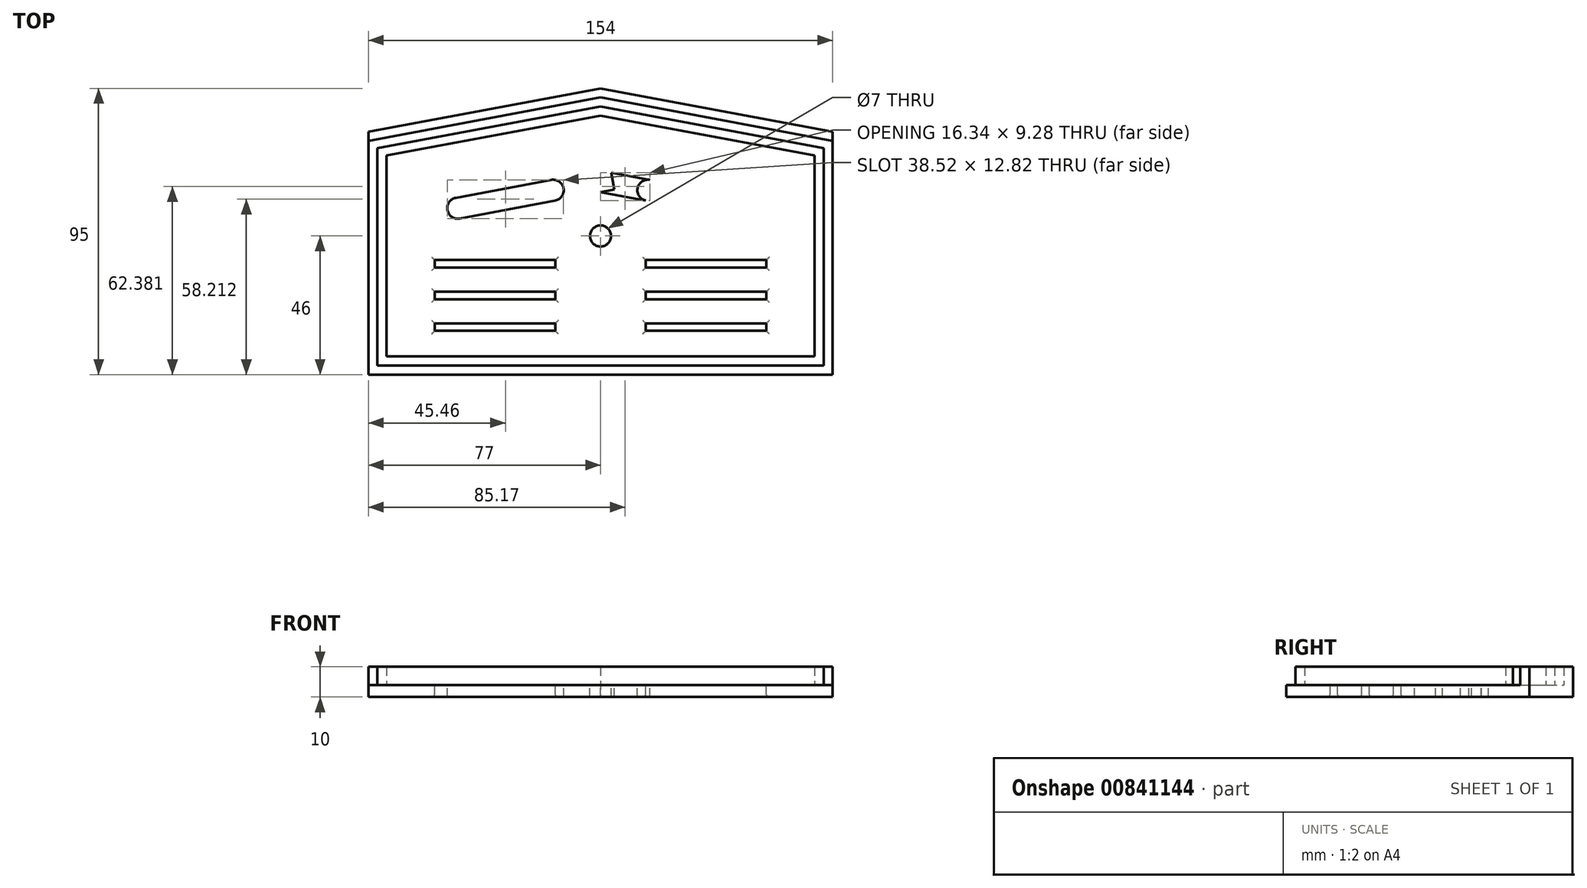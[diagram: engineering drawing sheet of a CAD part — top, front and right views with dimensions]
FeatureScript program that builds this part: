
annotation { "Feature Type Name" : "Feature", "Feature Type Description" : "" }
export const myFeature = defineFeature(function(context is Context, id is Id, definition is map)
    precondition{}
    {
        {
            var Q0;
            Q0=qCreatedBy(makeId("Top.planeOp"),FACE);
            var sketch = newSketch(context, id + "F0", { "sketchPlane" : qUnion([Q0])});
            skLineSegment(sketch, "E0.bottom", {"start": v(80, -49) * mm, "end": v(-80, -49) * mm});
            skLineSegment(sketch, "E0.top", {"start": v(80, 49) * mm, "end": v(-80, 49) * mm, "construction": true});
            skLineSegment(sketch, "E0.left", {"start": v(80, -49) * mm, "end": v(80, 49) * mm});
            skLineSegment(sketch, "E0.right", {"start": v(-80, -49) * mm, "end": v(-80, 49) * mm});
            skPoint(sketch, "E0.middle", {"position": v(0, 0) * mm});
            skLineSegment(sketch, "E1.bottom", {"start": v(-80, -49) * mm, "end": v(80, -49) * mm});
            skLineSegment(sketch, "E1.left", {"start": v(-80, -49) * mm, "end": v(-80, 85) * mm});
            skLineSegment(sketch, "E1.right", {"start": v(80, -49) * mm, "end": v(80, 43) * mm});
            skLineSegment(sketch, "E2.bottom", {"start": v(77, -46) * mm, "end": v(-77, -46) * mm});
            skLineSegment(sketch, "E2.top", {"start": v(77, 46) * mm, "end": v(-77, 46) * mm, "construction": true});
            skLineSegment(sketch, "E2.left", {"start": v(77, -46) * mm, "end": v(77, 46) * mm});
            skLineSegment(sketch, "E2.right", {"start": v(-77, -46) * mm, "end": v(-77, 46) * mm});
            skLineSegment(sketch, "E3.bottom", {"start": v(74, -43) * mm, "end": v(-74, -43) * mm});
            skLineSegment(sketch, "E3.top", {"start": v(74, 43) * mm, "end": v(-74, 43) * mm, "construction": true});
            skLineSegment(sketch, "E3.left", {"start": v(74, -43) * mm, "end": v(74, 43) * mm});
            skLineSegment(sketch, "E3.right", {"start": v(-74, -43) * mm, "end": v(-74, 43) * mm});
            skLineSegment(sketch, "E4.bottom", {"start": v(71, -40) * mm, "end": v(-71, -40) * mm});
            skLineSegment(sketch, "E4.top", {"start": v(71, 40) * mm, "end": v(-71, 40) * mm, "construction": true});
            skLineSegment(sketch, "E4.left", {"start": v(71, -40) * mm, "end": v(71, 40) * mm});
            skLineSegment(sketch, "E4.right", {"start": v(-71, -40) * mm, "end": v(-71, 40) * mm});
            skLineSegment(sketch, "E5.bottom", {"start": v(-80, 49) * mm, "end": v(80, 49) * mm, "construction": true});
            skLineSegment(sketch, "E5.top", {"start": v(-80, 34) * mm, "end": v(80, 34) * mm, "construction": true});
            skLineSegment(sketch, "E5.left", {"start": v(-80, 49) * mm, "end": v(-80, 34) * mm, "construction": true});
            skLineSegment(sketch, "E5.right", {"start": v(80, 49) * mm, "end": v(80, 34) * mm, "construction": true});
            skLineSegment(sketch, "E6", {"start": v(0, 49) * mm, "end": v(0, -49) * mm, "construction": true});
            skLineSegment(sketch, "E7", {"start": v(0, 49) * mm, "end": v(-80, 34) * mm});
            skLineSegment(sketch, "E8", {"start": v(0, 46) * mm, "end": v(-80, 31) * mm});
            skLineSegment(sketch, "E9", {"start": v(0, 43) * mm, "end": v(-80, 28) * mm});
            skLineSegment(sketch, "E10", {"start": v(0, 40) * mm, "end": v(-80, 25) * mm});
            skLineSegment(sketch, "E11", {"start": v(0, 49) * mm, "end": v(80, 34) * mm});
            skLineSegment(sketch, "E12", {"start": v(0, 46) * mm, "end": v(80, 31) * mm});
            skLineSegment(sketch, "E13", {"start": v(0, 43) * mm, "end": v(80, 28) * mm});
            skLineSegment(sketch, "E14", {"start": v(0, 40) * mm, "end": v(80, 25) * mm});
            skSolve(sketch);
        }
        {
            var Q0;
            {var subQ6=sQuery(id+"F0.wireOp",EDGE,"E4.bottom");Q0=makeQuery(id+"F0.imprint","IMPRINT",FACE,{"disambiguationData":[TD([[makeQuery(id+"F0.imprint","IMPRINT",EDGE,{"derivedFrom":subQ6}),-1.0]])]});}
            var Q1;
            {var subQ2=sQuery(id+"F0.wireOp",EDGE,"E2.bottom");Q1=makeQuery(id+"F0.imprint","IMPRINT",FACE,{"disambiguationData":[TD([[makeQuery(id+"F0.imprint","IMPRINT",EDGE,{"derivedFrom":subQ2}),-1.0]])]});}
            var Q2;
            {var subQ0=sQuery(id+"F0.wireOp",EDGE,"E13");var subQ9=sQuery(id+"F0.wireOp",EDGE,"E4.left");var subQ11=makeQuery(id+"F0.imprint","INTERSECT",VERTEX,{"derivedFrom":[subQ9,subQ0]});Q2=makeQuery(id+"F0.imprint","IMPRINT",FACE,{"disambiguationData":[TD([[makeQuery(id+"F0.imprint","IMPRINT",EDGE,{"disambiguationData":[TD([[subQ11,-1.0]])],"derivedFrom":subQ9}),1.0]])]});}
            var Q3;
            {var subQ2=sQuery(id+"F0.wireOp",EDGE,"E1.bottom");Q3=makeQuery(id+"F0.imprint","IMPRINT",FACE,{"disambiguationData":[TD([[makeQuery(id+"F0.imprint","IMPRINT",EDGE,{"derivedFrom":subQ2}),1.0]])]});}
            var Q4;
            {var subQ7=sQuery(id+"F0.wireOp",EDGE,"E3.bottom");Q4=makeQuery(id+"F0.imprint","IMPRINT",FACE,{"disambiguationData":[TD([[makeQuery(id+"F0.imprint","IMPRINT",EDGE,{"derivedFrom":subQ7}),-1.0]])]});}
            var Q5;
            {var subQ0=sQuery(id+"F0.wireOp",EDGE,"E8");var subQ1=sQuery(id+"F0.wireOp",EDGE,"E1.left");var subQ2=makeQuery(id+"F0.imprint","INTERSECT",VERTEX,{"derivedFrom":[subQ1,subQ0]});Q5=makeQuery(id+"F0.imprint","IMPRINT",FACE,{"disambiguationData":[TD([[makeQuery(id+"F0.imprint","IMPRINT",EDGE,{"disambiguationData":[TD([[subQ2,1.0]])],"derivedFrom":subQ1}),-1.0]])]});}
            var Q6;
            {var subQ0=sQuery(id+"F0.wireOp",EDGE,"E7");var subQ1=sQuery(id+"F0.wireOp",EDGE,"E1.left");var subQ2=makeQuery(id+"F0.imprint","INTERSECT",VERTEX,{"derivedFrom":[subQ1,subQ0]});Q6=makeQuery(id+"F0.imprint","IMPRINT",FACE,{"disambiguationData":[TD([[makeQuery(id+"F0.imprint","IMPRINT",EDGE,{"disambiguationData":[TD([[subQ2,1.0]])],"derivedFrom":subQ1}),-1.0]])]});}
            var Q7;
            {var subQ0=sQuery(id+"F0.wireOp",EDGE,"E9");var subQ1=sQuery(id+"F0.wireOp",EDGE,"E1.left");var subQ2=makeQuery(id+"F0.imprint","INTERSECT",VERTEX,{"derivedFrom":[subQ1,subQ0]});Q7=makeQuery(id+"F0.imprint","IMPRINT",FACE,{"disambiguationData":[TD([[makeQuery(id+"F0.imprint","IMPRINT",EDGE,{"disambiguationData":[TD([[subQ2,1.0]])],"derivedFrom":subQ1}),-1.0]])]});}
            var Q8;
            {var subQ0=sQuery(id+"F0.wireOp",EDGE,"E7");var subQ1=sQuery(id+"F0.wireOp",EDGE,"E2.right");var subQ2=makeQuery(id+"F0.imprint","INTERSECT",VERTEX,{"derivedFrom":[subQ1,subQ0]});Q8=makeQuery(id+"F0.imprint","IMPRINT",FACE,{"disambiguationData":[TD([[makeQuery(id+"F0.imprint","IMPRINT",EDGE,{"disambiguationData":[TD([[subQ2,1.0]])],"derivedFrom":subQ1}),-1.0]])]});}
            var Q9;
            {var subQ0=sQuery(id+"F0.wireOp",EDGE,"E9");var subQ1=sQuery(id+"F0.wireOp",EDGE,"E2.right");var subQ2=makeQuery(id+"F0.imprint","INTERSECT",VERTEX,{"derivedFrom":[subQ1,subQ0]});Q9=makeQuery(id+"F0.imprint","IMPRINT",FACE,{"disambiguationData":[TD([[makeQuery(id+"F0.imprint","IMPRINT",EDGE,{"disambiguationData":[TD([[subQ2,-1.0]])],"derivedFrom":subQ1}),-1.0]])]});}
            var Q10;
            {var subQ0=sQuery(id+"F0.wireOp",EDGE,"E10");var subQ1=sQuery(id+"F0.wireOp",EDGE,"E2.right");var subQ2=makeQuery(id+"F0.imprint","INTERSECT",VERTEX,{"derivedFrom":[subQ1,subQ0]});Q10=makeQuery(id+"F0.imprint","IMPRINT",FACE,{"disambiguationData":[TD([[makeQuery(id+"F0.imprint","IMPRINT",EDGE,{"disambiguationData":[TD([[subQ2,-1.0]])],"derivedFrom":subQ1}),-1.0]])]});}
            var Q11;
            {var subQ0=sQuery(id+"F0.wireOp",EDGE,"E9");var subQ1=sQuery(id+"F0.wireOp",EDGE,"E3.right");var subQ2=makeQuery(id+"F0.imprint","INTERSECT",VERTEX,{"derivedFrom":[subQ1,subQ0]});Q11=makeQuery(id+"F0.imprint","IMPRINT",FACE,{"disambiguationData":[TD([[makeQuery(id+"F0.imprint","IMPRINT",EDGE,{"disambiguationData":[TD([[subQ2,-1.0]])],"derivedFrom":subQ1}),-1.0]])]});}
            var Q12;
            {var subQ0=sQuery(id+"F0.wireOp",EDGE,"E10");var subQ1=sQuery(id+"F0.wireOp",EDGE,"E3.right");var subQ2=makeQuery(id+"F0.imprint","INTERSECT",VERTEX,{"derivedFrom":[subQ1,subQ0]});Q12=makeQuery(id+"F0.imprint","IMPRINT",FACE,{"disambiguationData":[TD([[makeQuery(id+"F0.imprint","IMPRINT",EDGE,{"disambiguationData":[TD([[subQ2,-1.0]])],"derivedFrom":subQ1}),-1.0]])]});}
            var Q13;
            {var subQ0=sQuery(id+"F0.wireOp",EDGE,"E7");var subQ1=sQuery(id+"F0.wireOp",EDGE,"E3.right");var subQ2=makeQuery(id+"F0.imprint","INTERSECT",VERTEX,{"derivedFrom":[subQ1,subQ0]});Q13=makeQuery(id+"F0.imprint","IMPRINT",FACE,{"disambiguationData":[TD([[makeQuery(id+"F0.imprint","IMPRINT",EDGE,{"disambiguationData":[TD([[subQ2,1.0]])],"derivedFrom":subQ1}),-1.0]])]});}
            var Q14;
            {var subQ7=sQuery(id+"F0.wireOp",EDGE,"E11");var subQ9=sQuery(id+"F0.wireOp",EDGE,"E4.left");var subQ10=makeQuery(id+"F0.imprint","INTERSECT",VERTEX,{"derivedFrom":[subQ9,subQ7]});Q14=makeQuery(id+"F0.imprint","IMPRINT",FACE,{"disambiguationData":[TD([[makeQuery(id+"F0.imprint","IMPRINT",EDGE,{"disambiguationData":[TD([[subQ10,1.0]])],"derivedFrom":subQ9}),1.0]])]});}
            var Q15;
            {var subQ0=sQuery(id+"F0.wireOp",EDGE,"E14");var subQ9=sQuery(id+"F0.wireOp",EDGE,"E4.left");var subQ10=makeQuery(id+"F0.imprint","INTERSECT",VERTEX,{"derivedFrom":[subQ9,subQ0]});Q15=makeQuery(id+"F0.imprint","IMPRINT",FACE,{"disambiguationData":[TD([[makeQuery(id+"F0.imprint","IMPRINT",EDGE,{"disambiguationData":[TD([[subQ10,-1.0]])],"derivedFrom":subQ9}),1.0]])]});}
            var Q16;
            {var subQ0=sQuery(id+"F0.wireOp",EDGE,"E11");var subQ1=sQuery(id+"F0.wireOp",EDGE,"E3.left");var subQ2=makeQuery(id+"F0.imprint","INTERSECT",VERTEX,{"derivedFrom":[subQ1,subQ0]});Q16=makeQuery(id+"F0.imprint","IMPRINT",FACE,{"disambiguationData":[TD([[makeQuery(id+"F0.imprint","IMPRINT",EDGE,{"disambiguationData":[TD([[subQ2,1.0]])],"derivedFrom":subQ1}),1.0]])]});}
            var Q17;
            {var subQ0=sQuery(id+"F0.wireOp",EDGE,"E11");var subQ1=sQuery(id+"F0.wireOp",EDGE,"E2.left");var subQ2=makeQuery(id+"F0.imprint","INTERSECT",VERTEX,{"derivedFrom":[subQ1,subQ0]});Q17=makeQuery(id+"F0.imprint","IMPRINT",FACE,{"disambiguationData":[TD([[makeQuery(id+"F0.imprint","IMPRINT",EDGE,{"disambiguationData":[TD([[subQ2,1.0]])],"derivedFrom":subQ1}),1.0]])]});}
            var Q18;
            {var subQ0=sQuery(id+"F0.wireOp",EDGE,"E11");var subQ1=sQuery(id+"F0.wireOp",EDGE,"E1.right");var subQ2=makeQuery(id+"F0.imprint","INTERSECT",VERTEX,{"derivedFrom":[subQ1,subQ0]});Q18=makeQuery(id+"F0.imprint","IMPRINT",FACE,{"disambiguationData":[TD([[makeQuery(id+"F0.imprint","IMPRINT",EDGE,{"disambiguationData":[TD([[subQ2,1.0]])],"derivedFrom":subQ1}),1.0]])]});}
            var Q19;
            {var subQ0=sQuery(id+"F0.wireOp",EDGE,"E12");var subQ1=sQuery(id+"F0.wireOp",EDGE,"E1.right");var subQ2=makeQuery(id+"F0.imprint","INTERSECT",VERTEX,{"derivedFrom":[subQ1,subQ0]});Q19=makeQuery(id+"F0.imprint","IMPRINT",FACE,{"disambiguationData":[TD([[makeQuery(id+"F0.imprint","IMPRINT",EDGE,{"disambiguationData":[TD([[subQ2,1.0]])],"derivedFrom":subQ1}),1.0]])]});}
            var Q20;
            {var subQ0=sQuery(id+"F0.wireOp",EDGE,"E13");var subQ1=sQuery(id+"F0.wireOp",EDGE,"E1.right");var subQ2=makeQuery(id+"F0.imprint","INTERSECT",VERTEX,{"derivedFrom":[subQ1,subQ0]});Q20=makeQuery(id+"F0.imprint","IMPRINT",FACE,{"disambiguationData":[TD([[makeQuery(id+"F0.imprint","IMPRINT",EDGE,{"disambiguationData":[TD([[subQ2,1.0]])],"derivedFrom":subQ1}),1.0]])]});}
            var Q21;
            {var subQ0=sQuery(id+"F0.wireOp",EDGE,"E14");var subQ1=sQuery(id+"F0.wireOp",EDGE,"E2.left");var subQ2=makeQuery(id+"F0.imprint","INTERSECT",VERTEX,{"derivedFrom":[subQ1,subQ0]});Q21=makeQuery(id+"F0.imprint","IMPRINT",FACE,{"disambiguationData":[TD([[makeQuery(id+"F0.imprint","IMPRINT",EDGE,{"disambiguationData":[TD([[subQ2,-1.0]])],"derivedFrom":subQ1}),1.0]])]});}
            var Q22;
            {var subQ0=sQuery(id+"F0.wireOp",EDGE,"E14");var subQ1=sQuery(id+"F0.wireOp",EDGE,"E3.left");var subQ2=makeQuery(id+"F0.imprint","INTERSECT",VERTEX,{"derivedFrom":[subQ1,subQ0]});Q22=makeQuery(id+"F0.imprint","IMPRINT",FACE,{"disambiguationData":[TD([[makeQuery(id+"F0.imprint","IMPRINT",EDGE,{"disambiguationData":[TD([[subQ2,-1.0]])],"derivedFrom":subQ1}),1.0]])]});}
            var Q23;
            {var subQ0=sQuery(id+"F0.wireOp",EDGE,"E13");var subQ1=sQuery(id+"F0.wireOp",EDGE,"E3.left");var subQ2=makeQuery(id+"F0.imprint","INTERSECT",VERTEX,{"derivedFrom":[subQ1,subQ0]});Q23=makeQuery(id+"F0.imprint","IMPRINT",FACE,{"disambiguationData":[TD([[makeQuery(id+"F0.imprint","IMPRINT",EDGE,{"disambiguationData":[TD([[subQ2,-1.0]])],"derivedFrom":subQ1}),1.0]])]});}
            var Q24;
            {var subQ0=sQuery(id+"F0.wireOp",EDGE,"E13");var subQ1=sQuery(id+"F0.wireOp",EDGE,"E2.left");var subQ2=makeQuery(id+"F0.imprint","INTERSECT",VERTEX,{"derivedFrom":[subQ1,subQ0]});Q24=makeQuery(id+"F0.imprint","IMPRINT",FACE,{"disambiguationData":[TD([[makeQuery(id+"F0.imprint","IMPRINT",EDGE,{"disambiguationData":[TD([[subQ2,-1.0]])],"derivedFrom":subQ1}),1.0]])]});}
            extrude(context, id + "F1", {"entities" : qUnion([Q0, Q1, Q2, Q3, Q4, Q5, Q6, Q7, Q8, Q9, Q10, Q11, Q12, Q13, Q14, Q15, Q16, Q17, Q18, Q19, Q20, Q21, Q22, Q23, Q24]), "depth" : 4 * mm, "offsetDistance" : 25 * mm});
        }
        {
            var Q0;
            {var subQ0=sQuery(id+"F0.wireOp",EDGE,"E11");var subQ1=sQuery(id+"F0.wireOp",EDGE,"E1.right");var subQ2=makeQuery(id+"F0.imprint","INTERSECT",VERTEX,{"derivedFrom":[subQ1,subQ0]});Q0=makeQuery(id+"F0.imprint","IMPRINT",FACE,{"disambiguationData":[TD([[makeQuery(id+"F0.imprint","IMPRINT",EDGE,{"disambiguationData":[TD([[subQ2,1.0]])],"derivedFrom":subQ1}),1.0]])]});}
            var Q1;
            {var subQ0=sQuery(id+"F0.wireOp",EDGE,"E11");var subQ1=sQuery(id+"F0.wireOp",EDGE,"E2.left");var subQ2=makeQuery(id+"F0.imprint","INTERSECT",VERTEX,{"derivedFrom":[subQ1,subQ0]});Q1=makeQuery(id+"F0.imprint","IMPRINT",FACE,{"disambiguationData":[TD([[makeQuery(id+"F0.imprint","IMPRINT",EDGE,{"disambiguationData":[TD([[subQ2,1.0]])],"derivedFrom":subQ1}),1.0]])]});}
            var Q2;
            {var subQ0=sQuery(id+"F0.wireOp",EDGE,"E11");var subQ1=sQuery(id+"F0.wireOp",EDGE,"E3.left");var subQ2=makeQuery(id+"F0.imprint","INTERSECT",VERTEX,{"derivedFrom":[subQ1,subQ0]});Q2=makeQuery(id+"F0.imprint","IMPRINT",FACE,{"disambiguationData":[TD([[makeQuery(id+"F0.imprint","IMPRINT",EDGE,{"disambiguationData":[TD([[subQ2,1.0]])],"derivedFrom":subQ1}),1.0]])]});}
            var Q3;
            {var subQ7=sQuery(id+"F0.wireOp",EDGE,"E11");var subQ9=sQuery(id+"F0.wireOp",EDGE,"E4.left");var subQ10=makeQuery(id+"F0.imprint","INTERSECT",VERTEX,{"derivedFrom":[subQ9,subQ7]});Q3=makeQuery(id+"F0.imprint","IMPRINT",FACE,{"disambiguationData":[TD([[makeQuery(id+"F0.imprint","IMPRINT",EDGE,{"disambiguationData":[TD([[subQ10,1.0]])],"derivedFrom":subQ9}),1.0]])]});}
            var Q4;
            {var subQ0=sQuery(id+"F0.wireOp",EDGE,"E7");var subQ1=sQuery(id+"F0.wireOp",EDGE,"E3.right");var subQ2=makeQuery(id+"F0.imprint","INTERSECT",VERTEX,{"derivedFrom":[subQ1,subQ0]});Q4=makeQuery(id+"F0.imprint","IMPRINT",FACE,{"disambiguationData":[TD([[makeQuery(id+"F0.imprint","IMPRINT",EDGE,{"disambiguationData":[TD([[subQ2,1.0]])],"derivedFrom":subQ1}),-1.0]])]});}
            var Q5;
            {var subQ0=sQuery(id+"F0.wireOp",EDGE,"E7");var subQ1=sQuery(id+"F0.wireOp",EDGE,"E2.right");var subQ2=makeQuery(id+"F0.imprint","INTERSECT",VERTEX,{"derivedFrom":[subQ1,subQ0]});Q5=makeQuery(id+"F0.imprint","IMPRINT",FACE,{"disambiguationData":[TD([[makeQuery(id+"F0.imprint","IMPRINT",EDGE,{"disambiguationData":[TD([[subQ2,1.0]])],"derivedFrom":subQ1}),-1.0]])]});}
            var Q6;
            {var subQ0=sQuery(id+"F0.wireOp",EDGE,"E7");var subQ1=sQuery(id+"F0.wireOp",EDGE,"E1.left");var subQ2=makeQuery(id+"F0.imprint","INTERSECT",VERTEX,{"derivedFrom":[subQ1,subQ0]});Q6=makeQuery(id+"F0.imprint","IMPRINT",FACE,{"disambiguationData":[TD([[makeQuery(id+"F0.imprint","IMPRINT",EDGE,{"disambiguationData":[TD([[subQ2,1.0]])],"derivedFrom":subQ1}),-1.0]])]});}
            var Q7;
            {var subQ0=sQuery(id+"F0.wireOp",EDGE,"E9");var subQ1=sQuery(id+"F0.wireOp",EDGE,"E1.left");var subQ2=makeQuery(id+"F0.imprint","INTERSECT",VERTEX,{"derivedFrom":[subQ1,subQ0]});Q7=makeQuery(id+"F0.imprint","IMPRINT",FACE,{"disambiguationData":[TD([[makeQuery(id+"F0.imprint","IMPRINT",EDGE,{"disambiguationData":[TD([[subQ2,1.0]])],"derivedFrom":subQ1}),-1.0]])]});}
            var Q8;
            {var subQ0=sQuery(id+"F0.wireOp",EDGE,"E10");var subQ1=sQuery(id+"F0.wireOp",EDGE,"E3.right");var subQ2=makeQuery(id+"F0.imprint","INTERSECT",VERTEX,{"derivedFrom":[subQ1,subQ0]});Q8=makeQuery(id+"F0.imprint","IMPRINT",FACE,{"disambiguationData":[TD([[makeQuery(id+"F0.imprint","IMPRINT",EDGE,{"disambiguationData":[TD([[subQ2,-1.0]])],"derivedFrom":subQ1}),-1.0]])]});}
            var Q9;
            {var subQ0=sQuery(id+"F0.wireOp",EDGE,"E14");var subQ9=sQuery(id+"F0.wireOp",EDGE,"E4.left");var subQ10=makeQuery(id+"F0.imprint","INTERSECT",VERTEX,{"derivedFrom":[subQ9,subQ0]});Q9=makeQuery(id+"F0.imprint","IMPRINT",FACE,{"disambiguationData":[TD([[makeQuery(id+"F0.imprint","IMPRINT",EDGE,{"disambiguationData":[TD([[subQ10,-1.0]])],"derivedFrom":subQ9}),1.0]])]});}
            var Q10;
            {var subQ0=sQuery(id+"F0.wireOp",EDGE,"E13");var subQ1=sQuery(id+"F0.wireOp",EDGE,"E1.right");var subQ2=makeQuery(id+"F0.imprint","INTERSECT",VERTEX,{"derivedFrom":[subQ1,subQ0]});Q10=makeQuery(id+"F0.imprint","IMPRINT",FACE,{"disambiguationData":[TD([[makeQuery(id+"F0.imprint","IMPRINT",EDGE,{"disambiguationData":[TD([[subQ2,1.0]])],"derivedFrom":subQ1}),1.0]])]});}
            var Q11;
            {var subQ0=sQuery(id+"F0.wireOp",EDGE,"E14");var subQ1=sQuery(id+"F0.wireOp",EDGE,"E3.left");var subQ2=makeQuery(id+"F0.imprint","INTERSECT",VERTEX,{"derivedFrom":[subQ1,subQ0]});Q11=makeQuery(id+"F0.imprint","IMPRINT",FACE,{"disambiguationData":[TD([[makeQuery(id+"F0.imprint","IMPRINT",EDGE,{"disambiguationData":[TD([[subQ2,-1.0]])],"derivedFrom":subQ1}),1.0]])]});}
            var Q12;
            {var subQ2=sQuery(id+"F0.wireOp",EDGE,"E1.bottom");Q12=makeQuery(id+"F0.imprint","IMPRINT",FACE,{"disambiguationData":[TD([[makeQuery(id+"F0.imprint","IMPRINT",EDGE,{"derivedFrom":subQ2}),1.0]])]});}
            var Q13;
            {var subQ7=sQuery(id+"F0.wireOp",EDGE,"E3.bottom");Q13=makeQuery(id+"F0.imprint","IMPRINT",FACE,{"disambiguationData":[TD([[makeQuery(id+"F0.imprint","IMPRINT",EDGE,{"derivedFrom":subQ7}),-1.0]])]});}
            var Q14;
            {var subQ0=sQuery(id+"F0.wireOp",EDGE,"E8");var subQ1=sQuery(id+"F0.wireOp",EDGE,"E1.left");var subQ2=makeQuery(id+"F0.imprint","INTERSECT",VERTEX,{"derivedFrom":[subQ1,subQ0]});Q14=makeQuery(id+"F0.imprint","IMPRINT",FACE,{"disambiguationData":[TD([[makeQuery(id+"F0.imprint","IMPRINT",EDGE,{"disambiguationData":[TD([[subQ2,1.0]])],"derivedFrom":subQ1}),-1.0]])]});}
            var Q15;
            {var subQ0=sQuery(id+"F0.wireOp",EDGE,"E12");var subQ1=sQuery(id+"F0.wireOp",EDGE,"E1.right");var subQ2=makeQuery(id+"F0.imprint","INTERSECT",VERTEX,{"derivedFrom":[subQ1,subQ0]});Q15=makeQuery(id+"F0.imprint","IMPRINT",FACE,{"disambiguationData":[TD([[makeQuery(id+"F0.imprint","IMPRINT",EDGE,{"disambiguationData":[TD([[subQ2,1.0]])],"derivedFrom":subQ1}),1.0]])]});}
            extrude(context, id + "F2", {"entities" : qUnion([Q0, Q1, Q2, Q3, Q4, Q5, Q6, Q7, Q8, Q9, Q10, Q11, Q12, Q13, Q14, Q15]), "operationType" : NewBodyOperationType.ADD, "depth" : 10 * mm, "offsetDistance" : 25 * mm});
        }
        {
            var Q0;
            Q0=makeQuery(id+"F2.boolean.opBoolean","SPLIT",FACE,{"disambiguationData":[TD([makeQuery(id+"F2.opExtrude","SWEPT_FACE",FACE,{"disambiguationData":[OSD([sQuery(id+"F0.wireOp",EDGE,"E4.bottom")])]})])],"derivedFrom":makeQuery(id+"F1.opExtrude","CAP_FACE",FACE,{"disambiguationData":[OSD([sQuery(id+"F0.wireOp",EDGE,"E1.bottom"),sQuery(id+"F0.wireOp",EDGE,"E1.left"),sQuery(id+"F0.wireOp",EDGE,"E1.right"),sQuery(id+"F0.wireOp",EDGE,"E7"),sQuery(id+"F0.wireOp",EDGE,"E11")])],"isStart":false})});
            var sketch = newSketch(context, id + "F3", { "sketchPlane" : qUnion([Q0])});
            skLineSegment(sketch, "E15", {"start": v(0, 0) * mm, "end": v(0, 40) * mm});
            skLineSegment(sketch, "E16", {"start": v(0, 40) * mm, "end": v(-71, 26.69) * mm});
            skLineSegment(sketch, "E17", {"start": v(-71, 26.69) * mm, "end": v(-71, 0) * mm});
            skLineSegment(sketch, "E18", {"start": v(-71, 0) * mm, "end": v(0, 0) * mm});
            skCircle(sketch, "E19", {"center": v(0, 0) * mm, "radius": 3.5 * mm});
            skLineSegment(sketch, "E20", {"start": v(-71, 26.69) * mm, "end": v(-67.68, 9) * mm});
            skLineSegment(sketch, "E21", {"start": v(0, 40) * mm, "end": v(3.32, 22.3) * mm});
            skLineSegment(sketch, "E22", {"start": v(3.32, 22.3) * mm, "end": v(-67.68, 9) * mm});
            skLineSegment(sketch, "E23", {"start": v(-67.68, 9) * mm, "end": v(-66.4, 2.12) * mm});
            skLineSegment(sketch, "E24", {"start": v(-66.4, 2.12) * mm, "end": v(4.6, 15.43) * mm});
            skLineSegment(sketch, "E25", {"start": v(4.6, 15.43) * mm, "end": v(3.32, 22.3) * mm});
            skLineSegment(sketch, "E26", {"start": v(-48.03, 12.68) * mm, "end": v(-46.74, 5.8) * mm});
            skLineSegment(sketch, "E27", {"start": v(-16.34, 18.62) * mm, "end": v(-15.05, 11.74) * mm});
            skArc(sketch, "E28", {"start": v(-48.03, 12.68) * mm, "mid": v(-50.8, 8.6) * mm, "end": v(-46.74, 5.8) * mm});
            skArc(sketch, "E29", {"start": v(-15.05, 11.74) * mm, "mid": v(-12.28, 15.82) * mm, "end": v(-16.34, 18.62) * mm});
            skArc(sketch, "E30.MirrorCS", {"start": v(15.05, 11.74) * mm, "mid": v(12.28, 15.82) * mm, "end": v(16.34, 18.62) * mm});
            skLineSegment(sketch, "E31.MirrorCS", {"start": v(-3.32, 22.3) * mm, "end": v(67.68, 9) * mm});
            skArc(sketch, "E32.MirrorCS", {"start": v(48.03, 12.68) * mm, "mid": v(50.8, 8.6) * mm, "end": v(46.74, 5.8) * mm});
            skLineSegment(sketch, "E33.MirrorCS", {"start": v(66.4, 2.12) * mm, "end": v(-4.6, 15.43) * mm});
            skSolve(sketch);
        }
        {
            var Q0;
            {var subQ0=sQuery(id+"F3.wireOp",EDGE,"E18");var subQ1=sQuery(id+"F3.wireOp",EDGE,"E15");var subQ2=makeQuery(id+"F3.imprint","INTERSECT",VERTEX,{"derivedFrom":[subQ1,subQ0]});Q0=makeQuery(id+"F3.imprint","IMPRINT",FACE,{"disambiguationData":[TD([[makeQuery(id+"F3.imprint","IMPRINT",EDGE,{"disambiguationData":[TD([[subQ2,-1.0]])],"derivedFrom":subQ1}),1.0]])]});}
            var Q1;
            {var subQ0=sQuery(id+"F3.wireOp",EDGE,"E18");var subQ1=sQuery(id+"F3.wireOp",EDGE,"E15");var subQ2=makeQuery(id+"F3.imprint","INTERSECT",VERTEX,{"derivedFrom":[subQ1,subQ0]});Q1=makeQuery(id+"F3.imprint","IMPRINT",FACE,{"disambiguationData":[TD([[makeQuery(id+"F3.imprint","IMPRINT",EDGE,{"disambiguationData":[TD([[subQ2,-1.0]])],"derivedFrom":subQ1}),-1.0]])]});}
            extrude(context, id + "F4", {"entities" : qUnion([Q0, Q1]), "operationType" : NewBodyOperationType.REMOVE, "oppositeDirection" : true, "depth" : 25 * mm, "offsetDistance" : 25 * mm});
        }
        {
            var Q0;
            Q0=makeQuery(id+"F3.imprint","IMPRINT",FACE,{"disambiguationData":[TD([[makeQuery(id+"F3.imprint","IMPRINT",EDGE,{"derivedFrom":sQuery(id+"F3.wireOp",EDGE,"E26")}),-1.0]])]});
            var Q1;
            {var subQ1=sQuery(id+"F3.wireOp",EDGE,"E26");Q1=makeQuery(id+"F3.imprint","IMPRINT",FACE,{"disambiguationData":[TD([[makeQuery(id+"F3.imprint","IMPRINT",EDGE,{"derivedFrom":subQ1}),1.0]])]});}
            var Q2;
            Q2=makeQuery(id+"F3.imprint","IMPRINT",FACE,{"disambiguationData":[TD([[makeQuery(id+"F3.imprint","IMPRINT",EDGE,{"derivedFrom":sQuery(id+"F3.wireOp",EDGE,"E27")}),1.0]])]});
            var Q3;
            {var subQ0=sQuery(id+"F3.wireOp",EDGE,"E30.MirrorCS");Q3=makeQuery(id+"F3.imprint","IMPRINT",FACE,{"disambiguationData":[TD([[makeQuery(id+"F3.imprint","IMPRINT",EDGE,{"derivedFrom":subQ0}),-1.0]])]});}
            extrude(context, id + "F5", {"entities" : qUnion([Q0, Q1, Q2, Q3]), "operationType" : NewBodyOperationType.REMOVE, "oppositeDirection" : true, "depth" : 5 * mm, "offsetDistance" : 25 * mm});
        }
        {
            var Q0;
            {var subQ17=sQuery(id+"F3.wireOp",EDGE,"E21");Q0=makeQuery(id+"F3.imprint","IMPRINT",FACE,{"disambiguationData":[TD([[makeQuery(id+"F3.imprint","IMPRINT",EDGE,{"derivedFrom":subQ17}),1.0]])]});}
            var sketch = newSketch(context, id + "F6", { "sketchPlane" : qUnion([Q0])});
            skLineSegment(sketch, "E34.bottom", {"start": v(-55, -18.5) * mm, "end": v(-15, -18.5) * mm});
            skLineSegment(sketch, "E34.top", {"start": v(-55, -21) * mm, "end": v(-15, -21) * mm});
            skLineSegment(sketch, "E34.left", {"start": v(-55, -18.5) * mm, "end": v(-55, -21) * mm});
            skLineSegment(sketch, "E34.right", {"start": v(-15, -18.5) * mm, "end": v(-15, -21) * mm});
            skLineSegment(sketch, "E35", {"start": v(-15, -21) * mm, "end": v(0, -21) * mm});
            skLineSegment(sketch, "E36", {"start": v(-68.1, -25) * mm, "end": v(84.03, -25) * mm});
            skLineSegment(sketch, "E37.MirrorCS", {"start": v(-55, -29) * mm, "end": v(-15, -29) * mm});
            skLineSegment(sketch, "E38.MirrorCS", {"start": v(-55, -31.5) * mm, "end": v(-15, -31.5) * mm});
            skLineSegment(sketch, "E39.MirrorCS", {"start": v(-55, -31.5) * mm, "end": v(-55, -29) * mm});
            skLineSegment(sketch, "E40.MirrorCS", {"start": v(-15, -31.5) * mm, "end": v(-15, -29) * mm});
            skLineSegment(sketch, "E41.MirrorCS", {"start": v(15, -31.5) * mm, "end": v(15, -29) * mm});
            skLineSegment(sketch, "E42.MirrorCS", {"start": v(55, -31.5) * mm, "end": v(55, -29) * mm});
            skLineSegment(sketch, "E43.MirrorCS", {"start": v(55, -31.5) * mm, "end": v(15, -31.5) * mm});
            skLineSegment(sketch, "E44.MirrorCS", {"start": v(55, -29) * mm, "end": v(15, -29) * mm});
            skLineSegment(sketch, "E45.MirrorCS", {"start": v(55, -18.5) * mm, "end": v(55, -21) * mm});
            skLineSegment(sketch, "E46.MirrorCS", {"start": v(55, -18.5) * mm, "end": v(15, -18.5) * mm});
            skLineSegment(sketch, "E47.MirrorCS", {"start": v(55, -21) * mm, "end": v(15, -21) * mm});
            skLineSegment(sketch, "E48.MirrorCS", {"start": v(15, -18.5) * mm, "end": v(15, -21) * mm});
            skLineSegment(sketch, "E49", {"start": v(-66.87, -14.5) * mm, "end": v(85.27, -14.5) * mm});
            skLineSegment(sketch, "E50.MirrorCS", {"start": v(55, -10.5) * mm, "end": v(55, -8) * mm});
            skLineSegment(sketch, "E51.MirrorCS", {"start": v(15, -10.5) * mm, "end": v(15, -8) * mm});
            skLineSegment(sketch, "E52.MirrorCS", {"start": v(55, -10.5) * mm, "end": v(15, -10.5) * mm});
            skLineSegment(sketch, "E53.MirrorCS", {"start": v(55, -8) * mm, "end": v(15, -8) * mm});
            skLineSegment(sketch, "E54.MirrorCS", {"start": v(-55, -10.5) * mm, "end": v(-55, -8) * mm});
            skLineSegment(sketch, "E55.MirrorCS", {"start": v(-15, -10.5) * mm, "end": v(-15, -8) * mm});
            skLineSegment(sketch, "E56.MirrorCS", {"start": v(-55, -8) * mm, "end": v(-15, -8) * mm});
            skLineSegment(sketch, "E57.MirrorCS", {"start": v(-55, -10.5) * mm, "end": v(-15, -10.5) * mm});
            skSolve(sketch);
        }
        {
            var Q0;
            Q0=makeQuery(id+"F6.imprint","IMPRINT",FACE,{"disambiguationData":[TD([[makeQuery(id+"F6.imprint","IMPRINT",EDGE,{"derivedFrom":sQuery(id+"F6.wireOp",EDGE,"E37.MirrorCS")}),-1.0]])]});
            var Q1;
            Q1=makeQuery(id+"F6.imprint","IMPRINT",FACE,{"disambiguationData":[TD([[makeQuery(id+"F6.imprint","IMPRINT",EDGE,{"derivedFrom":sQuery(id+"F6.wireOp",EDGE,"E34.bottom")}),-1.0]])]});
            var Q2;
            Q2=makeQuery(id+"F6.imprint","IMPRINT",FACE,{"disambiguationData":[TD([[makeQuery(id+"F6.imprint","IMPRINT",EDGE,{"derivedFrom":sQuery(id+"F6.wireOp",EDGE,"E45.MirrorCS")}),-1.0]])]});
            var Q3;
            Q3=makeQuery(id+"F6.imprint","IMPRINT",FACE,{"disambiguationData":[TD([[makeQuery(id+"F6.imprint","IMPRINT",EDGE,{"derivedFrom":sQuery(id+"F6.wireOp",EDGE,"E41.MirrorCS")}),-1.0]])]});
            var Q4;
            Q4=makeQuery(id+"F6.imprint","IMPRINT",FACE,{"disambiguationData":[TD([[makeQuery(id+"F6.imprint","IMPRINT",EDGE,{"derivedFrom":sQuery(id+"F6.wireOp",EDGE,"E54.MirrorCS")}),-1.0]])]});
            var Q5;
            Q5=makeQuery(id+"F6.imprint","IMPRINT",FACE,{"disambiguationData":[TD([[makeQuery(id+"F6.imprint","IMPRINT",EDGE,{"derivedFrom":sQuery(id+"F6.wireOp",EDGE,"E50.MirrorCS")}),1.0]])]});
            extrude(context, id + "F7", {"entities" : qUnion([Q0, Q1, Q2, Q3, Q4, Q5]), "operationType" : NewBodyOperationType.REMOVE, "oppositeDirection" : true, "depth" : 25 * mm, "offsetDistance" : 25 * mm});
        }
        {
            var Q0;
            Q0=makeQuery(id+"F7.boolean.opBoolean","COPY",EDGE,{"derivedFrom":makeQuery(id+"F7.opExtrude","CAP_EDGE",EDGE,{"disambiguationData":[OSD([sQuery(id+"F6.wireOp",EDGE,"E38.MirrorCS")])],"isStart":true})});
            var Q1;
            Q1=makeQuery(id+"F7.boolean.opBoolean","COPY",EDGE,{"derivedFrom":makeQuery(id+"F7.opExtrude","CAP_EDGE",EDGE,{"disambiguationData":[OSD([sQuery(id+"F6.wireOp",EDGE,"E37.MirrorCS")])],"isStart":true})});
            var Q2;
            Q2=makeQuery(id+"F7.boolean.opBoolean","COPY",EDGE,{"derivedFrom":makeQuery(id+"F7.opExtrude","CAP_EDGE",EDGE,{"disambiguationData":[OSD([sQuery(id+"F6.wireOp",EDGE,"E34.top")])],"isStart":true})});
            var Q3;
            Q3=makeQuery(id+"F7.boolean.opBoolean","COPY",EDGE,{"derivedFrom":makeQuery(id+"F7.opExtrude","CAP_EDGE",EDGE,{"disambiguationData":[OSD([sQuery(id+"F6.wireOp",EDGE,"E34.bottom")])],"isStart":true})});
            var Q4;
            Q4=makeQuery(id+"F7.boolean.opBoolean","COPY",EDGE,{"derivedFrom":makeQuery(id+"F7.opExtrude","CAP_EDGE",EDGE,{"disambiguationData":[OSD([sQuery(id+"F6.wireOp",EDGE,"E57.MirrorCS")])],"isStart":true})});
            var Q5;
            Q5=makeQuery(id+"F7.boolean.opBoolean","COPY",EDGE,{"derivedFrom":makeQuery(id+"F7.opExtrude","CAP_EDGE",EDGE,{"disambiguationData":[OSD([sQuery(id+"F6.wireOp",EDGE,"E56.MirrorCS")])],"isStart":true})});
            var Q6;
            Q6=makeQuery(id+"F7.boolean.opBoolean","COPY",EDGE,{"derivedFrom":makeQuery(id+"F7.opExtrude","CAP_EDGE",EDGE,{"disambiguationData":[OSD([sQuery(id+"F6.wireOp",EDGE,"E54.MirrorCS")])],"isStart":true})});
            var Q7;
            Q7=makeQuery(id+"F7.boolean.opBoolean","COPY",EDGE,{"derivedFrom":makeQuery(id+"F7.opExtrude","CAP_EDGE",EDGE,{"disambiguationData":[OSD([sQuery(id+"F6.wireOp",EDGE,"E34.left")])],"isStart":true})});
            var Q8;
            Q8=makeQuery(id+"F7.boolean.opBoolean","COPY",EDGE,{"derivedFrom":makeQuery(id+"F7.opExtrude","CAP_EDGE",EDGE,{"disambiguationData":[OSD([sQuery(id+"F6.wireOp",EDGE,"E39.MirrorCS")])],"isStart":true})});
            var Q9;
            Q9=makeQuery(id+"F7.boolean.opBoolean","COPY",EDGE,{"derivedFrom":makeQuery(id+"F7.opExtrude","CAP_EDGE",EDGE,{"disambiguationData":[OSD([sQuery(id+"F6.wireOp",EDGE,"E40.MirrorCS")])],"isStart":true})});
            var Q10;
            Q10=makeQuery(id+"F7.boolean.opBoolean","COPY",EDGE,{"derivedFrom":makeQuery(id+"F7.opExtrude","CAP_EDGE",EDGE,{"disambiguationData":[OSD([sQuery(id+"F6.wireOp",EDGE,"E34.right")])],"isStart":true})});
            var Q11;
            Q11=makeQuery(id+"F7.boolean.opBoolean","COPY",EDGE,{"derivedFrom":makeQuery(id+"F7.opExtrude","CAP_EDGE",EDGE,{"disambiguationData":[OSD([sQuery(id+"F6.wireOp",EDGE,"E55.MirrorCS")])],"isStart":true})});
            var Q12;
            Q12=makeQuery(id+"F7.boolean.opBoolean","COPY",EDGE,{"derivedFrom":makeQuery(id+"F7.opExtrude","CAP_EDGE",EDGE,{"disambiguationData":[OSD([sQuery(id+"F6.wireOp",EDGE,"E51.MirrorCS")])],"isStart":true})});
            var Q13;
            Q13=makeQuery(id+"F7.boolean.opBoolean","COPY",EDGE,{"derivedFrom":makeQuery(id+"F7.opExtrude","CAP_EDGE",EDGE,{"disambiguationData":[OSD([sQuery(id+"F6.wireOp",EDGE,"E48.MirrorCS")])],"isStart":true})});
            var Q14;
            Q14=makeQuery(id+"F7.boolean.opBoolean","COPY",EDGE,{"derivedFrom":makeQuery(id+"F7.opExtrude","CAP_EDGE",EDGE,{"disambiguationData":[OSD([sQuery(id+"F6.wireOp",EDGE,"E41.MirrorCS")])],"isStart":true})});
            var Q15;
            Q15=makeQuery(id+"F7.boolean.opBoolean","COPY",EDGE,{"derivedFrom":makeQuery(id+"F7.opExtrude","CAP_EDGE",EDGE,{"disambiguationData":[OSD([sQuery(id+"F6.wireOp",EDGE,"E44.MirrorCS")])],"isStart":true})});
            var Q16;
            Q16=makeQuery(id+"F7.boolean.opBoolean","COPY",EDGE,{"derivedFrom":makeQuery(id+"F7.opExtrude","CAP_EDGE",EDGE,{"disambiguationData":[OSD([sQuery(id+"F6.wireOp",EDGE,"E43.MirrorCS")])],"isStart":true})});
            var Q17;
            Q17=makeQuery(id+"F7.boolean.opBoolean","COPY",EDGE,{"derivedFrom":makeQuery(id+"F7.opExtrude","CAP_EDGE",EDGE,{"disambiguationData":[OSD([sQuery(id+"F6.wireOp",EDGE,"E46.MirrorCS")])],"isStart":true})});
            var Q18;
            Q18=makeQuery(id+"F7.boolean.opBoolean","INTERSECT",EDGE,{"derivedFrom":[makeQuery(id+"F1.opExtrude","CAP_FACE",FACE,{"disambiguationData":[OSD([sQuery(id+"F0.wireOp",EDGE,"E1.bottom"),sQuery(id+"F0.wireOp",EDGE,"E1.left"),sQuery(id+"F0.wireOp",EDGE,"E1.right"),sQuery(id+"F0.wireOp",EDGE,"E7"),sQuery(id+"F0.wireOp",EDGE,"E11")])],"isStart":true}),makeQuery(id+"F7.opExtrude","SWEPT_FACE",FACE,{"disambiguationData":[OSD([sQuery(id+"F6.wireOp",EDGE,"E51.MirrorCS")])]})]});
            var Q19;
            Q19=makeQuery(id+"F7.boolean.opBoolean","INTERSECT",EDGE,{"derivedFrom":[makeQuery(id+"F1.opExtrude","CAP_FACE",FACE,{"disambiguationData":[OSD([sQuery(id+"F0.wireOp",EDGE,"E1.bottom"),sQuery(id+"F0.wireOp",EDGE,"E1.left"),sQuery(id+"F0.wireOp",EDGE,"E1.right"),sQuery(id+"F0.wireOp",EDGE,"E7"),sQuery(id+"F0.wireOp",EDGE,"E11")])],"isStart":true}),makeQuery(id+"F7.opExtrude","SWEPT_FACE",FACE,{"disambiguationData":[OSD([sQuery(id+"F6.wireOp",EDGE,"E48.MirrorCS")])]})]});
            var Q20;
            Q20=makeQuery(id+"F7.boolean.opBoolean","INTERSECT",EDGE,{"derivedFrom":[makeQuery(id+"F1.opExtrude","CAP_FACE",FACE,{"disambiguationData":[OSD([sQuery(id+"F0.wireOp",EDGE,"E1.bottom"),sQuery(id+"F0.wireOp",EDGE,"E1.left"),sQuery(id+"F0.wireOp",EDGE,"E1.right"),sQuery(id+"F0.wireOp",EDGE,"E7"),sQuery(id+"F0.wireOp",EDGE,"E11")])],"isStart":true}),makeQuery(id+"F7.opExtrude","SWEPT_FACE",FACE,{"disambiguationData":[OSD([sQuery(id+"F6.wireOp",EDGE,"E43.MirrorCS")])]})]});
            var Q21;
            Q21=makeQuery(id+"F7.boolean.opBoolean","INTERSECT",EDGE,{"derivedFrom":[makeQuery(id+"F1.opExtrude","CAP_FACE",FACE,{"disambiguationData":[OSD([sQuery(id+"F0.wireOp",EDGE,"E1.bottom"),sQuery(id+"F0.wireOp",EDGE,"E1.left"),sQuery(id+"F0.wireOp",EDGE,"E1.right"),sQuery(id+"F0.wireOp",EDGE,"E7"),sQuery(id+"F0.wireOp",EDGE,"E11")])],"isStart":true}),makeQuery(id+"F7.opExtrude","SWEPT_FACE",FACE,{"disambiguationData":[OSD([sQuery(id+"F6.wireOp",EDGE,"E41.MirrorCS")])]})]});
            var Q22;
            Q22=makeQuery(id+"F7.boolean.opBoolean","INTERSECT",EDGE,{"derivedFrom":[makeQuery(id+"F1.opExtrude","CAP_FACE",FACE,{"disambiguationData":[OSD([sQuery(id+"F0.wireOp",EDGE,"E1.bottom"),sQuery(id+"F0.wireOp",EDGE,"E1.left"),sQuery(id+"F0.wireOp",EDGE,"E1.right"),sQuery(id+"F0.wireOp",EDGE,"E7"),sQuery(id+"F0.wireOp",EDGE,"E11")])],"isStart":true}),makeQuery(id+"F7.opExtrude","SWEPT_FACE",FACE,{"disambiguationData":[OSD([sQuery(id+"F6.wireOp",EDGE,"E44.MirrorCS")])]})]});
            var Q23;
            Q23=makeQuery(id+"F7.boolean.opBoolean","INTERSECT",EDGE,{"derivedFrom":[makeQuery(id+"F1.opExtrude","CAP_FACE",FACE,{"disambiguationData":[OSD([sQuery(id+"F0.wireOp",EDGE,"E1.bottom"),sQuery(id+"F0.wireOp",EDGE,"E1.left"),sQuery(id+"F0.wireOp",EDGE,"E1.right"),sQuery(id+"F0.wireOp",EDGE,"E7"),sQuery(id+"F0.wireOp",EDGE,"E11")])],"isStart":true}),makeQuery(id+"F7.opExtrude","SWEPT_FACE",FACE,{"disambiguationData":[OSD([sQuery(id+"F6.wireOp",EDGE,"E47.MirrorCS")])]})]});
            var Q24;
            Q24=makeQuery(id+"F7.boolean.opBoolean","INTERSECT",EDGE,{"derivedFrom":[makeQuery(id+"F1.opExtrude","CAP_FACE",FACE,{"disambiguationData":[OSD([sQuery(id+"F0.wireOp",EDGE,"E1.bottom"),sQuery(id+"F0.wireOp",EDGE,"E1.left"),sQuery(id+"F0.wireOp",EDGE,"E1.right"),sQuery(id+"F0.wireOp",EDGE,"E7"),sQuery(id+"F0.wireOp",EDGE,"E11")])],"isStart":true}),makeQuery(id+"F7.opExtrude","SWEPT_FACE",FACE,{"disambiguationData":[OSD([sQuery(id+"F6.wireOp",EDGE,"E46.MirrorCS")])]})]});
            var Q25;
            Q25=makeQuery(id+"F7.boolean.opBoolean","INTERSECT",EDGE,{"derivedFrom":[makeQuery(id+"F1.opExtrude","CAP_FACE",FACE,{"disambiguationData":[OSD([sQuery(id+"F0.wireOp",EDGE,"E1.bottom"),sQuery(id+"F0.wireOp",EDGE,"E1.left"),sQuery(id+"F0.wireOp",EDGE,"E1.right"),sQuery(id+"F0.wireOp",EDGE,"E7"),sQuery(id+"F0.wireOp",EDGE,"E11")])],"isStart":true}),makeQuery(id+"F7.opExtrude","SWEPT_FACE",FACE,{"disambiguationData":[OSD([sQuery(id+"F6.wireOp",EDGE,"E53.MirrorCS")])]})]});
            var Q26;
            Q26=makeQuery(id+"F7.boolean.opBoolean","INTERSECT",EDGE,{"derivedFrom":[makeQuery(id+"F1.opExtrude","CAP_FACE",FACE,{"disambiguationData":[OSD([sQuery(id+"F0.wireOp",EDGE,"E1.bottom"),sQuery(id+"F0.wireOp",EDGE,"E1.left"),sQuery(id+"F0.wireOp",EDGE,"E1.right"),sQuery(id+"F0.wireOp",EDGE,"E7"),sQuery(id+"F0.wireOp",EDGE,"E11")])],"isStart":true}),makeQuery(id+"F7.opExtrude","SWEPT_FACE",FACE,{"disambiguationData":[OSD([sQuery(id+"F6.wireOp",EDGE,"E52.MirrorCS")])]})]});
            var Q27;
            Q27=makeQuery(id+"F7.boolean.opBoolean","INTERSECT",EDGE,{"derivedFrom":[makeQuery(id+"F1.opExtrude","CAP_FACE",FACE,{"disambiguationData":[OSD([sQuery(id+"F0.wireOp",EDGE,"E1.bottom"),sQuery(id+"F0.wireOp",EDGE,"E1.left"),sQuery(id+"F0.wireOp",EDGE,"E1.right"),sQuery(id+"F0.wireOp",EDGE,"E7"),sQuery(id+"F0.wireOp",EDGE,"E11")])],"isStart":true}),makeQuery(id+"F7.opExtrude","SWEPT_FACE",FACE,{"disambiguationData":[OSD([sQuery(id+"F6.wireOp",EDGE,"E42.MirrorCS")])]})]});
            var Q28;
            Q28=makeQuery(id+"F7.boolean.opBoolean","INTERSECT",EDGE,{"derivedFrom":[makeQuery(id+"F1.opExtrude","CAP_FACE",FACE,{"disambiguationData":[OSD([sQuery(id+"F0.wireOp",EDGE,"E1.bottom"),sQuery(id+"F0.wireOp",EDGE,"E1.left"),sQuery(id+"F0.wireOp",EDGE,"E1.right"),sQuery(id+"F0.wireOp",EDGE,"E7"),sQuery(id+"F0.wireOp",EDGE,"E11")])],"isStart":true}),makeQuery(id+"F7.opExtrude","SWEPT_FACE",FACE,{"disambiguationData":[OSD([sQuery(id+"F6.wireOp",EDGE,"E45.MirrorCS")])]})]});
            var Q29;
            Q29=makeQuery(id+"F7.boolean.opBoolean","INTERSECT",EDGE,{"derivedFrom":[makeQuery(id+"F1.opExtrude","CAP_FACE",FACE,{"disambiguationData":[OSD([sQuery(id+"F0.wireOp",EDGE,"E1.bottom"),sQuery(id+"F0.wireOp",EDGE,"E1.left"),sQuery(id+"F0.wireOp",EDGE,"E1.right"),sQuery(id+"F0.wireOp",EDGE,"E7"),sQuery(id+"F0.wireOp",EDGE,"E11")])],"isStart":true}),makeQuery(id+"F7.opExtrude","SWEPT_FACE",FACE,{"disambiguationData":[OSD([sQuery(id+"F6.wireOp",EDGE,"E50.MirrorCS")])]})]});
            var Q30;
            Q30=makeQuery(id+"F7.boolean.opBoolean","INTERSECT",EDGE,{"derivedFrom":[makeQuery(id+"F1.opExtrude","CAP_FACE",FACE,{"disambiguationData":[OSD([sQuery(id+"F0.wireOp",EDGE,"E1.bottom"),sQuery(id+"F0.wireOp",EDGE,"E1.left"),sQuery(id+"F0.wireOp",EDGE,"E1.right"),sQuery(id+"F0.wireOp",EDGE,"E7"),sQuery(id+"F0.wireOp",EDGE,"E11")])],"isStart":true}),makeQuery(id+"F7.opExtrude","SWEPT_FACE",FACE,{"disambiguationData":[OSD([sQuery(id+"F6.wireOp",EDGE,"E40.MirrorCS")])]})]});
            var Q31;
            Q31=makeQuery(id+"F7.boolean.opBoolean","INTERSECT",EDGE,{"derivedFrom":[makeQuery(id+"F1.opExtrude","CAP_FACE",FACE,{"disambiguationData":[OSD([sQuery(id+"F0.wireOp",EDGE,"E1.bottom"),sQuery(id+"F0.wireOp",EDGE,"E1.left"),sQuery(id+"F0.wireOp",EDGE,"E1.right"),sQuery(id+"F0.wireOp",EDGE,"E7"),sQuery(id+"F0.wireOp",EDGE,"E11")])],"isStart":true}),makeQuery(id+"F7.opExtrude","SWEPT_FACE",FACE,{"disambiguationData":[OSD([sQuery(id+"F6.wireOp",EDGE,"E34.right")])]})]});
            var Q32;
            Q32=makeQuery(id+"F7.boolean.opBoolean","INTERSECT",EDGE,{"derivedFrom":[makeQuery(id+"F1.opExtrude","CAP_FACE",FACE,{"disambiguationData":[OSD([sQuery(id+"F0.wireOp",EDGE,"E1.bottom"),sQuery(id+"F0.wireOp",EDGE,"E1.left"),sQuery(id+"F0.wireOp",EDGE,"E1.right"),sQuery(id+"F0.wireOp",EDGE,"E7"),sQuery(id+"F0.wireOp",EDGE,"E11")])],"isStart":true}),makeQuery(id+"F7.opExtrude","SWEPT_FACE",FACE,{"disambiguationData":[OSD([sQuery(id+"F6.wireOp",EDGE,"E39.MirrorCS")])]})]});
            var Q33;
            Q33=makeQuery(id+"F7.boolean.opBoolean","INTERSECT",EDGE,{"derivedFrom":[makeQuery(id+"F1.opExtrude","CAP_FACE",FACE,{"disambiguationData":[OSD([sQuery(id+"F0.wireOp",EDGE,"E1.bottom"),sQuery(id+"F0.wireOp",EDGE,"E1.left"),sQuery(id+"F0.wireOp",EDGE,"E1.right"),sQuery(id+"F0.wireOp",EDGE,"E7"),sQuery(id+"F0.wireOp",EDGE,"E11")])],"isStart":true}),makeQuery(id+"F7.opExtrude","SWEPT_FACE",FACE,{"disambiguationData":[OSD([sQuery(id+"F6.wireOp",EDGE,"E34.left")])]})]});
            var Q34;
            Q34=makeQuery(id+"F7.boolean.opBoolean","INTERSECT",EDGE,{"derivedFrom":[makeQuery(id+"F1.opExtrude","CAP_FACE",FACE,{"disambiguationData":[OSD([sQuery(id+"F0.wireOp",EDGE,"E1.bottom"),sQuery(id+"F0.wireOp",EDGE,"E1.left"),sQuery(id+"F0.wireOp",EDGE,"E1.right"),sQuery(id+"F0.wireOp",EDGE,"E7"),sQuery(id+"F0.wireOp",EDGE,"E11")])],"isStart":true}),makeQuery(id+"F7.opExtrude","SWEPT_FACE",FACE,{"disambiguationData":[OSD([sQuery(id+"F6.wireOp",EDGE,"E54.MirrorCS")])]})]});
            var Q35;
            Q35=makeQuery(id+"F7.boolean.opBoolean","INTERSECT",EDGE,{"derivedFrom":[makeQuery(id+"F1.opExtrude","CAP_FACE",FACE,{"disambiguationData":[OSD([sQuery(id+"F0.wireOp",EDGE,"E1.bottom"),sQuery(id+"F0.wireOp",EDGE,"E1.left"),sQuery(id+"F0.wireOp",EDGE,"E1.right"),sQuery(id+"F0.wireOp",EDGE,"E7"),sQuery(id+"F0.wireOp",EDGE,"E11")])],"isStart":true}),makeQuery(id+"F7.opExtrude","SWEPT_FACE",FACE,{"disambiguationData":[OSD([sQuery(id+"F6.wireOp",EDGE,"E34.top")])]})]});
            var Q36;
            Q36=makeQuery(id+"F7.boolean.opBoolean","INTERSECT",EDGE,{"derivedFrom":[makeQuery(id+"F1.opExtrude","CAP_FACE",FACE,{"disambiguationData":[OSD([sQuery(id+"F0.wireOp",EDGE,"E1.bottom"),sQuery(id+"F0.wireOp",EDGE,"E1.left"),sQuery(id+"F0.wireOp",EDGE,"E1.right"),sQuery(id+"F0.wireOp",EDGE,"E7"),sQuery(id+"F0.wireOp",EDGE,"E11")])],"isStart":true}),makeQuery(id+"F7.opExtrude","SWEPT_FACE",FACE,{"disambiguationData":[OSD([sQuery(id+"F6.wireOp",EDGE,"E37.MirrorCS")])]})]});
            var Q37;
            Q37=makeQuery(id+"F7.boolean.opBoolean","INTERSECT",EDGE,{"derivedFrom":[makeQuery(id+"F1.opExtrude","CAP_FACE",FACE,{"disambiguationData":[OSD([sQuery(id+"F0.wireOp",EDGE,"E1.bottom"),sQuery(id+"F0.wireOp",EDGE,"E1.left"),sQuery(id+"F0.wireOp",EDGE,"E1.right"),sQuery(id+"F0.wireOp",EDGE,"E7"),sQuery(id+"F0.wireOp",EDGE,"E11")])],"isStart":true}),makeQuery(id+"F7.opExtrude","SWEPT_FACE",FACE,{"disambiguationData":[OSD([sQuery(id+"F6.wireOp",EDGE,"E38.MirrorCS")])]})]});
            var Q38;
            Q38=makeQuery(id+"F7.boolean.opBoolean","INTERSECT",EDGE,{"derivedFrom":[makeQuery(id+"F1.opExtrude","CAP_FACE",FACE,{"disambiguationData":[OSD([sQuery(id+"F0.wireOp",EDGE,"E1.bottom"),sQuery(id+"F0.wireOp",EDGE,"E1.left"),sQuery(id+"F0.wireOp",EDGE,"E1.right"),sQuery(id+"F0.wireOp",EDGE,"E7"),sQuery(id+"F0.wireOp",EDGE,"E11")])],"isStart":true}),makeQuery(id+"F7.opExtrude","SWEPT_FACE",FACE,{"disambiguationData":[OSD([sQuery(id+"F6.wireOp",EDGE,"E57.MirrorCS")])]})]});
            var Q39;
            Q39=makeQuery(id+"F7.boolean.opBoolean","INTERSECT",EDGE,{"derivedFrom":[makeQuery(id+"F1.opExtrude","CAP_FACE",FACE,{"disambiguationData":[OSD([sQuery(id+"F0.wireOp",EDGE,"E1.bottom"),sQuery(id+"F0.wireOp",EDGE,"E1.left"),sQuery(id+"F0.wireOp",EDGE,"E1.right"),sQuery(id+"F0.wireOp",EDGE,"E7"),sQuery(id+"F0.wireOp",EDGE,"E11")])],"isStart":true}),makeQuery(id+"F7.opExtrude","SWEPT_FACE",FACE,{"disambiguationData":[OSD([sQuery(id+"F6.wireOp",EDGE,"E56.MirrorCS")])]})]});
            var Q40;
            Q40=makeQuery(id+"F7.boolean.opBoolean","INTERSECT",EDGE,{"derivedFrom":[makeQuery(id+"F1.opExtrude","CAP_FACE",FACE,{"disambiguationData":[OSD([sQuery(id+"F0.wireOp",EDGE,"E1.bottom"),sQuery(id+"F0.wireOp",EDGE,"E1.left"),sQuery(id+"F0.wireOp",EDGE,"E1.right"),sQuery(id+"F0.wireOp",EDGE,"E7"),sQuery(id+"F0.wireOp",EDGE,"E11")])],"isStart":true}),makeQuery(id+"F7.opExtrude","SWEPT_FACE",FACE,{"disambiguationData":[OSD([sQuery(id+"F6.wireOp",EDGE,"E34.bottom")])]})]});
            var Q41;
            Q41=makeQuery(id+"F7.boolean.opBoolean","INTERSECT",EDGE,{"derivedFrom":[makeQuery(id+"F1.opExtrude","CAP_FACE",FACE,{"disambiguationData":[OSD([sQuery(id+"F0.wireOp",EDGE,"E1.bottom"),sQuery(id+"F0.wireOp",EDGE,"E1.left"),sQuery(id+"F0.wireOp",EDGE,"E1.right"),sQuery(id+"F0.wireOp",EDGE,"E7"),sQuery(id+"F0.wireOp",EDGE,"E11")])],"isStart":true}),makeQuery(id+"F7.opExtrude","SWEPT_FACE",FACE,{"disambiguationData":[OSD([sQuery(id+"F6.wireOp",EDGE,"E55.MirrorCS")])]})]});
            var Q42;
            Q42=makeQuery(id+"F7.boolean.opBoolean","COPY",EDGE,{"derivedFrom":makeQuery(id+"F7.opExtrude","CAP_EDGE",EDGE,{"disambiguationData":[OSD([sQuery(id+"F6.wireOp",EDGE,"E42.MirrorCS")])],"isStart":true})});
            var Q43;
            Q43=makeQuery(id+"F7.boolean.opBoolean","COPY",EDGE,{"derivedFrom":makeQuery(id+"F7.opExtrude","CAP_EDGE",EDGE,{"disambiguationData":[OSD([sQuery(id+"F6.wireOp",EDGE,"E45.MirrorCS")])],"isStart":true})});
            var Q44;
            Q44=makeQuery(id+"F7.boolean.opBoolean","COPY",EDGE,{"derivedFrom":makeQuery(id+"F7.opExtrude","CAP_EDGE",EDGE,{"disambiguationData":[OSD([sQuery(id+"F6.wireOp",EDGE,"E47.MirrorCS")])],"isStart":true})});
            var Q45;
            Q45=makeQuery(id+"F7.boolean.opBoolean","COPY",EDGE,{"derivedFrom":makeQuery(id+"F7.opExtrude","CAP_EDGE",EDGE,{"disambiguationData":[OSD([sQuery(id+"F6.wireOp",EDGE,"E52.MirrorCS")])],"isStart":true})});
            var Q46;
            Q46=makeQuery(id+"F7.boolean.opBoolean","COPY",EDGE,{"derivedFrom":makeQuery(id+"F7.opExtrude","CAP_EDGE",EDGE,{"disambiguationData":[OSD([sQuery(id+"F6.wireOp",EDGE,"E53.MirrorCS")])],"isStart":true})});
            var Q47;
            Q47=makeQuery(id+"F7.boolean.opBoolean","COPY",EDGE,{"derivedFrom":makeQuery(id+"F7.opExtrude","CAP_EDGE",EDGE,{"disambiguationData":[OSD([sQuery(id+"F6.wireOp",EDGE,"E50.MirrorCS")])],"isStart":true})});
            fillet(context, id + "F8", {"entities" : qUnion([Q0, Q1, Q2, Q3, Q4, Q5, Q6, Q7, Q8, Q9, Q10, Q11, Q12, Q13, Q14, Q15, Q16, Q17, Q18, Q19, Q20, Q21, Q22, Q23, Q24, Q25, Q26, Q27, Q28, Q29, Q30, Q31, Q32, Q33, Q34, Q35, Q36, Q37, Q38, Q39, Q40, Q41, Q42, Q43, Q44, Q45, Q46, Q47]), "radius" : 1 * mm, "tangentPropagation" : true, "allowEdgeOverflow" : false});
        }
    });
